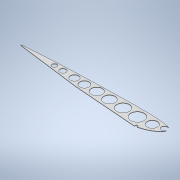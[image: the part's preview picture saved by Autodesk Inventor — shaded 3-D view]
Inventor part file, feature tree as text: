
AUTODESK INVENTOR PART (.ipt)
format: ipt  version: 2022 (Build 260153000, 153)  size: 221,696 bytes
history: native  units: mm
features: extrude x1, sketch x1
ambient origin geometry x8: Origin, YZ Plane, XZ Plane, XY Plane, X Axis, Y Axis, Z Axis, Center Point
bodies: Body1 (feature_tree)
feature tree (2):
  extrude  "Extrusion4"  Depth=1.0mm
  sketch  "Sketch1"  dims[d8=160.0mm d26=5.0mm d27=5.0mm d31=34.456mm d36=5.0mm d37=5.0mm d50=368.759386mm d51=15.0mm d52=28.0mm d53=31.0mm d54=27.0mm d57=15.0mm d59=33.0mm d61=23.0mm d62=20.0mm d63=1.0mm d64=0.0mm d65=44.669323mm d66=25.0mm d67=12.0mm d68=160.0mm d69=8.0mm]
